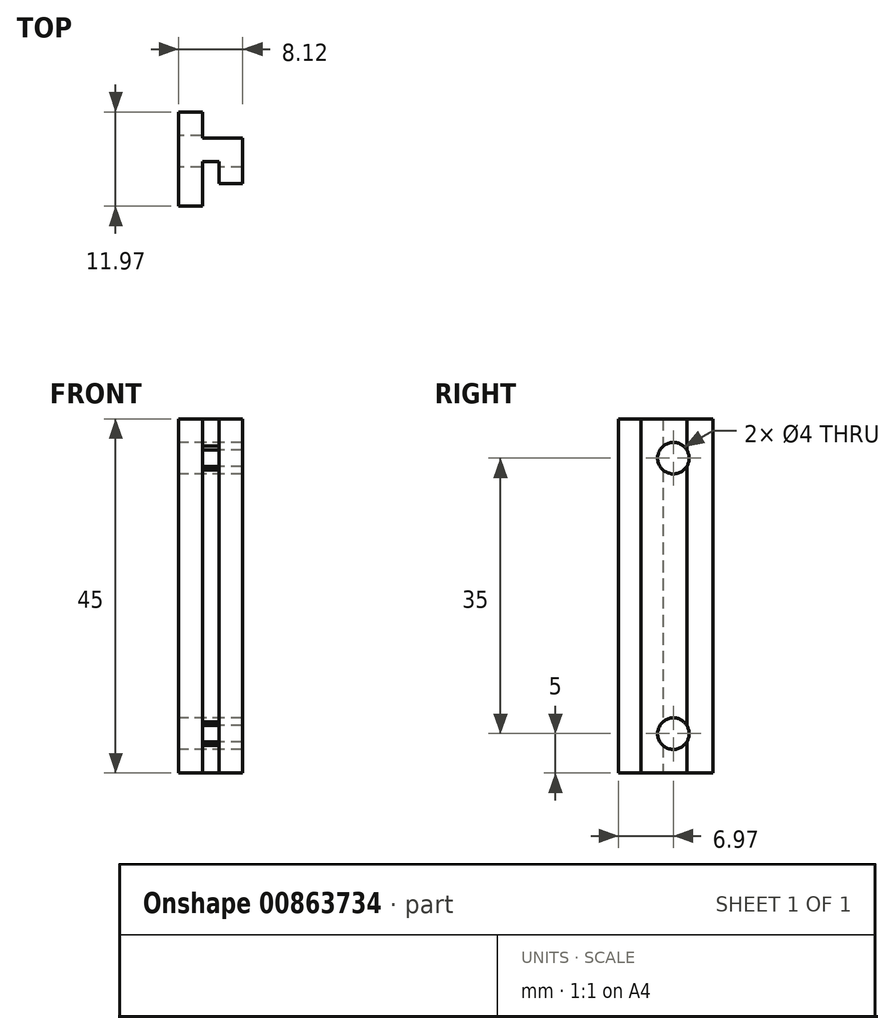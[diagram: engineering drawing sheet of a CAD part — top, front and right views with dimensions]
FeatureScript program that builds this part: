
annotation { "Feature Type Name" : "Feature", "Feature Type Description" : "" }
export const myFeature = defineFeature(function(context is Context, id is Id, definition is map)
    precondition{}
    {
        {
            var Q0;
            Q0=qCreatedBy(makeId("Top.planeOp"),FACE);
            var sketch = newSketch(context, id + "F0", { "sketchPlane" : qUnion([Q0])});
            skLineSegment(sketch, "E0", {"start": v(0, 0) * mm, "end": v(0, 11.97) * mm});
            skLineSegment(sketch, "E1", {"start": v(0, 11.97) * mm, "end": v(3, 11.97) * mm});
            skLineSegment(sketch, "E2", {"start": v(3, 11.97) * mm, "end": v(3, 8.67) * mm});
            skLineSegment(sketch, "E3", {"start": v(3, 8.67) * mm, "end": v(8.12, 8.67) * mm});
            skLineSegment(sketch, "E4", {"start": v(8.12, 8.67) * mm, "end": v(8.12, 2.88) * mm});
            skLineSegment(sketch, "E5", {"start": v(8.12, 2.88) * mm, "end": v(5.12, 2.88) * mm});
            skLineSegment(sketch, "E6", {"start": v(5.12, 2.88) * mm, "end": v(5.12, 5.67) * mm});
            skLineSegment(sketch, "E7", {"start": v(5.12, 5.67) * mm, "end": v(3, 5.67) * mm});
            skLineSegment(sketch, "E8", {"start": v(3, 5.67) * mm, "end": v(3, 0) * mm});
            skLineSegment(sketch, "E9", {"start": v(3, 0) * mm, "end": v(0, 0) * mm});
            skSolve(sketch);
        }
        {
            var Q0;
            Q0 = qSketchRegion(id + "F0", true);
            extrude(context, id + "F1", {"entities" : qUnion([Q0]), "depth" : 45 * mm, "offsetDistance" : 25 * mm});
        }
        {
            var Q0;
            Q0=makeQuery(id+"F1.opExtrude","SWEPT_FACE",FACE,{"disambiguationData":[OSD([sQuery(id+"F0.wireOp",EDGE,"E0")])]});
            var sketch = newSketch(context, id + "F2", { "sketchPlane" : qUnion([Q0])});
            skCircle(sketch, "E10", {"center": v(-6.97, 5) * mm, "radius": 2 * mm});
            skCircle(sketch, "E11", {"center": v(-6.97, 40) * mm, "radius": 2 * mm});
            skLineSegment(sketch, "E12", {"start": v(-6.97, 40) * mm, "end": v(-6.97, 5) * mm, "construction": true});
            skSolve(sketch);
        }
        {
            var Q0;
            Q0 = qSketchRegion(id + "F2", true);
            extrude(context, id + "F3", {"entities" : qUnion([Q0]), "operationType" : NewBodyOperationType.REMOVE, "endBound" : BoundingType.THROUGH_ALL, "oppositeDirection" : true, "depth" : 25 * mm, "offsetDistance" : 25 * mm});
        }
    });
